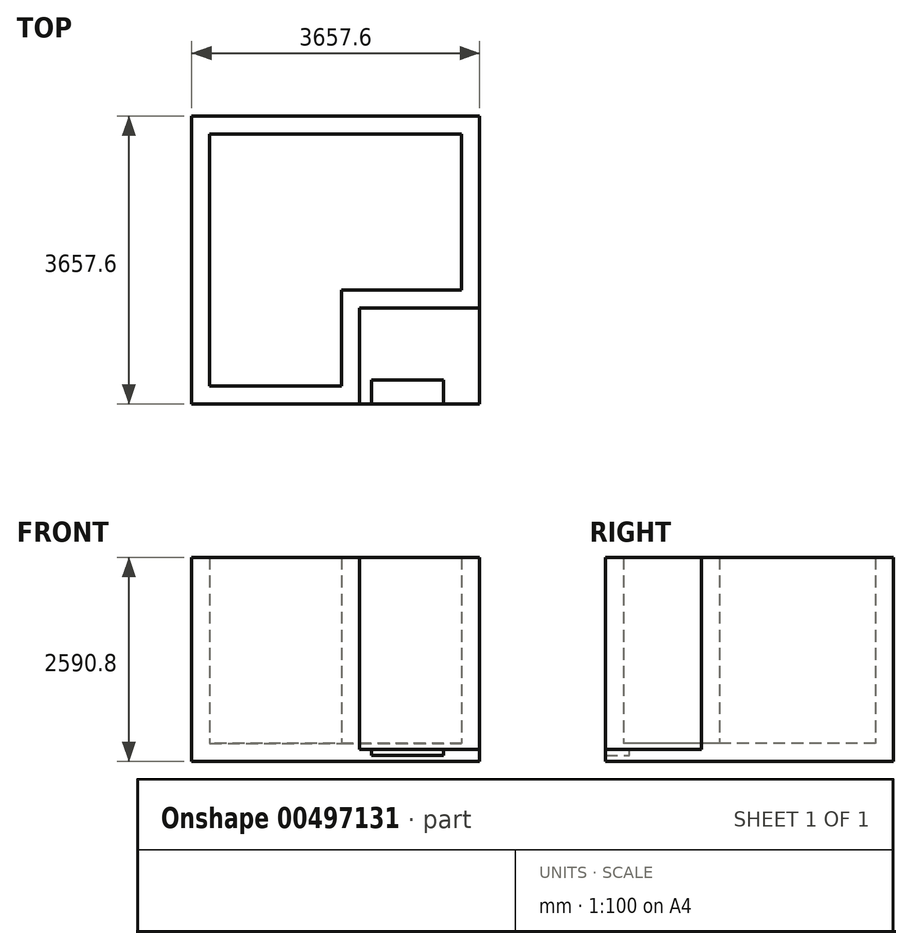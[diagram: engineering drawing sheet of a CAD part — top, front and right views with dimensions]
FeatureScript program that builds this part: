
annotation { "Feature Type Name" : "Feature", "Feature Type Description" : "" }
export const myFeature = defineFeature(function(context is Context, id is Id, definition is map)
    precondition{}
    {
        {
            var Q0;
            Q0=qCreatedBy(makeId("Top.planeOp"),FACE);
            var sketch = newSketch(context, id + "F0", { "sketchPlane" : qUnion([Q0])});
            skLineSegment(sketch, "E0", {"start": v(-1887.88, 1673.56) * mm, "end": v(-1887.88, -1984.04) * mm});
            skLineSegment(sketch, "E1", {"start": v(-1887.88, -1984.04) * mm, "end": v(245.72, -1984.04) * mm});
            skLineSegment(sketch, "E2", {"start": v(245.72, -1984.04) * mm, "end": v(245.72, -764.84) * mm});
            skLineSegment(sketch, "E3", {"start": v(245.72, -764.84) * mm, "end": v(1769.72, -764.84) * mm});
            skLineSegment(sketch, "E4", {"start": v(1769.72, -764.84) * mm, "end": v(1769.72, 1673.56) * mm});
            skLineSegment(sketch, "E5", {"start": v(1769.72, 1673.56) * mm, "end": v(-1887.88, 1673.56) * mm});
            skSolve(sketch);
        }
        {
            var Q0;
            Q0=makeQuery(id+"F0.imprint","IMPRINT",FACE,{"disambiguationData":[TD([[makeQuery(id+"F0.imprint","IMPRINT",EDGE,{"derivedFrom":sQuery(id+"F0.wireOp",EDGE,"E0")}),1.0]])]});
            extrude(context, id + "F1", {"entities" : qUnion([Q0]), "depth" : 2438.4 * mm});
        }
        {
            var Q0;
            Q0=makeQuery(id+"F1.opExtrude","CAP_FACE",FACE,{"disambiguationData":[OSD([sQuery(id+"F0.wireOp",EDGE,"E0"),sQuery(id+"F0.wireOp",EDGE,"E1"),sQuery(id+"F0.wireOp",EDGE,"E2"),sQuery(id+"F0.wireOp",EDGE,"E3"),sQuery(id+"F0.wireOp",EDGE,"E4"),sQuery(id+"F0.wireOp",EDGE,"E5")])],"isStart":true});
            var sketch = newSketch(context, id + "F2", { "sketchPlane" : qUnion([Q0])});
            skLineSegment(sketch, "E6.bottom", {"start": v(-1887.88, -1673.56) * mm, "end": v(1769.72, -1673.56) * mm});
            skLineSegment(sketch, "E6.top", {"start": v(-1887.88, 1984.04) * mm, "end": v(1769.72, 1984.04) * mm});
            skLineSegment(sketch, "E6.left", {"start": v(-1887.88, -1673.56) * mm, "end": v(-1887.88, 1984.04) * mm});
            skLineSegment(sketch, "E6.right", {"start": v(1769.72, -1673.56) * mm, "end": v(1769.72, 1984.04) * mm});
            skSolve(sketch);
        }
        {
            var Q0;
            {var subQ1=makeQuery(id+"F1.opExtrude","CAP_EDGE",EDGE,{"disambiguationData":[OSD([sQuery(id+"F0.wireOp",EDGE,"E2")])],"isStart":true});Q0=makeQuery(id+"F2.imprint","IMPRINT",FACE,{"disambiguationData":[TD([[makeQuery(id+"F2.imprint","IMPRINT",EDGE,{"derivedFrom":subQ1}),1.0]])]});}
            var Q1;
            {var subQ2=sQuery(id+"F2.wireOp",EDGE,"E6.bottom");Q1=makeQuery(id+"F2.imprint","IMPRINT",FACE,{"disambiguationData":[TD([[makeQuery(id+"F2.imprint","IMPRINT",EDGE,{"derivedFrom":subQ2}),-1.0]])]});}
            extrude(context, id + "F3", {"entities" : qUnion([Q0, Q1]), "operationType" : NewBodyOperationType.ADD, "depth" : 152.4 * mm});
        }
        {
            var Q0;
            Q0=makeQuery(id+"F1.opExtrude","CAP_FACE",FACE,{"disambiguationData":[OSD([sQuery(id+"F0.wireOp",EDGE,"E0"),sQuery(id+"F0.wireOp",EDGE,"E1"),sQuery(id+"F0.wireOp",EDGE,"E2"),sQuery(id+"F0.wireOp",EDGE,"E3"),sQuery(id+"F0.wireOp",EDGE,"E4"),sQuery(id+"F0.wireOp",EDGE,"E5")])],"isStart":false});
            shell(context, id + "F4", {"entities" : qUnion([Q0]), "thickness" : 228.6 * mm});
        }
        {
            var Q0;
            Q0=makeQuery(id+"F3.opExtrude","CAP_FACE",FACE,{"disambiguationData":[OSD([sQuery(id+"F2.wireOp",EDGE,"E6.bottom"),sQuery(id+"F2.wireOp",EDGE,"E6.top"),sQuery(id+"F2.wireOp",EDGE,"E6.left"),sQuery(id+"F2.wireOp",EDGE,"E6.right")])],"isStart":true});
            var sketch = newSketch(context, id + "F5", { "sketchPlane" : qUnion([Q0])});
            skLineSegment(sketch, "E7", {"start": v(245.72, -1984.04) * mm, "end": v(398.12, -1984.04) * mm});
            skLineSegment(sketch, "E8", {"start": v(398.12, -1984.04) * mm, "end": v(398.12, -1679.24) * mm});
            skLineSegment(sketch, "E9", {"start": v(398.12, -1679.24) * mm, "end": v(1312.52, -1679.24) * mm});
            skLineSegment(sketch, "E10", {"start": v(1312.52, -1679.24) * mm, "end": v(1312.52, -1984.04) * mm});
            skLineSegment(sketch, "E11", {"start": v(1312.52, -1984.04) * mm, "end": v(398.12, -1984.04) * mm});
            skLineSegment(sketch, "E12", {"start": v(398.12, -1984.04) * mm, "end": v(1312.52, -1984.04) * mm});
            skSolve(sketch);
        }
        {
            var Q0;
            Q0=makeQuery(id+"F5.imprint","IMPRINT",FACE,{"disambiguationData":[TD([[makeQuery(id+"F5.imprint","IMPRINT",EDGE,{"derivedFrom":sQuery(id+"F5.wireOp",EDGE,"E8")}),-1.0]])]});
            extrude(context, id + "F6", {"entities" : qUnion([Q0]), "operationType" : NewBodyOperationType.REMOVE, "oppositeDirection" : true, "depth" : 76.2 * mm});
        }
    });
